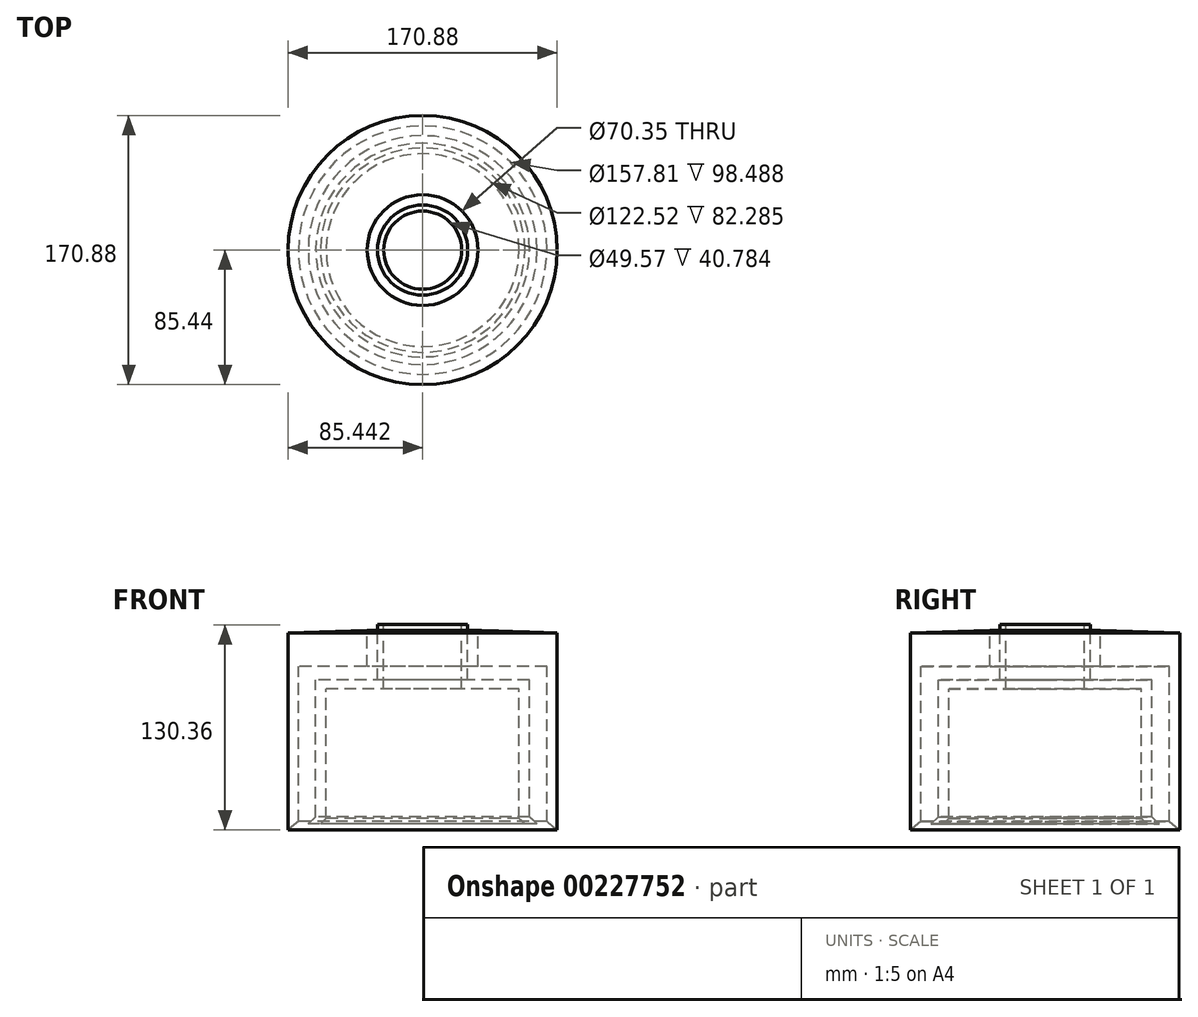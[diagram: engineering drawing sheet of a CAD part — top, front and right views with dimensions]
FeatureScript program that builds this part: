
annotation { "Feature Type Name" : "Feature", "Feature Type Description" : "" }
export const myFeature = defineFeature(function(context is Context, id is Id, definition is map)
    precondition{}
    {
        {
            var Q0;
            Q0=qCreatedBy(makeId("Front.planeOp"),FACE);
            var sketch = newSketch(context, id + "F0", { "sketchPlane" : qUnion([Q0])});
            skLineSegment(sketch, "E0", {"start": v(-12.46, 64.36) * mm, "end": v(-12.46, 41.48) * mm});
            skLineSegment(sketch, "E1", {"start": v(-12.46, 41.48) * mm, "end": v(-56.2, 41.48) * mm});
            skLineSegment(sketch, "E2", {"start": v(-56.2, 41.48) * mm, "end": v(-56.2, -57) * mm});
            skLineSegment(sketch, "E3", {"start": v(-56.2, -57) * mm, "end": v(-62.73, -62.32) * mm});
            skLineSegment(sketch, "E4", {"start": v(-62.73, -62.32) * mm, "end": v(-62.73, 62.73) * mm});
            skLineSegment(sketch, "E5", {"start": v(-62.73, 62.73) * mm, "end": v(-12.46, 64.36) * mm});
            skLineSegment(sketch, "E6", {"start": v(-5.93, 68.04) * mm, "end": v(-5.93, 32.9) * mm});
            skLineSegment(sketch, "E7", {"start": v(-5.93, 32.9) * mm, "end": v(-45.16, 32.9) * mm});
            skLineSegment(sketch, "E8", {"start": v(-45.16, 32.9) * mm, "end": v(-45.16, -53.94) * mm});
            skLineSegment(sketch, "E9", {"start": v(-45.16, -53.94) * mm, "end": v(-49.96, -58.44) * mm});
            skLineSegment(sketch, "E10", {"start": v(-49.96, -58.44) * mm, "end": v(-42.2, -58.44) * mm});
            skLineSegment(sketch, "E11", {"start": v(-42.2, -58.44) * mm, "end": v(-38.55, -55.03) * mm});
            skLineSegment(sketch, "E12", {"start": v(-38.55, -55.03) * mm, "end": v(-38.55, 27.26) * mm});
            skLineSegment(sketch, "E13", {"start": v(-38.55, 27.26) * mm, "end": v(-2.07, 27.26) * mm});
            skLineSegment(sketch, "E14", {"start": v(-2.07, 27.26) * mm, "end": v(-2.07, 68.04) * mm});
            skLineSegment(sketch, "E15", {"start": v(-2.07, 68.04) * mm, "end": v(-5.93, 68.04) * mm});
            skSolve(sketch);
        }
        {
            var Q0;
            Q0=qCreatedBy(makeId("Front.planeOp"),FACE);
            var sketch = newSketch(context, id + "F1", { "sketchPlane" : qUnion([Q0])});
            skLineSegment(sketch, "E16", {"start": v(22.71, 72.21) * mm, "end": v(22.71, -58.76) * mm, "construction": true});
            skSolve(sketch);
        }
        {
            var Q0;
            Q0=makeQuery(id+"F0.imprint","IMPRINT",FACE,{"disambiguationData":[TD([[makeQuery(id+"F0.imprint","IMPRINT",EDGE,{"derivedFrom":sQuery(id+"F0.wireOp",EDGE,"E0")}),-1.0]])]});
            var Q1;
            Q1=makeQuery(id+"F0.imprint","IMPRINT",FACE,{"disambiguationData":[TD([[makeQuery(id+"F0.imprint","IMPRINT",EDGE,{"derivedFrom":sQuery(id+"F0.wireOp",EDGE,"E6")}),1.0]])]});
            var Q2;
            Q2=sQuery(id+"F1.wireOp",EDGE,"E16");
            revolve(context, id + "F2", {"entities" : qUnion([Q0, Q1]), "axis" : qUnion([Q2]), "revolveType" : RevolveType.FULL});
        }
    });
